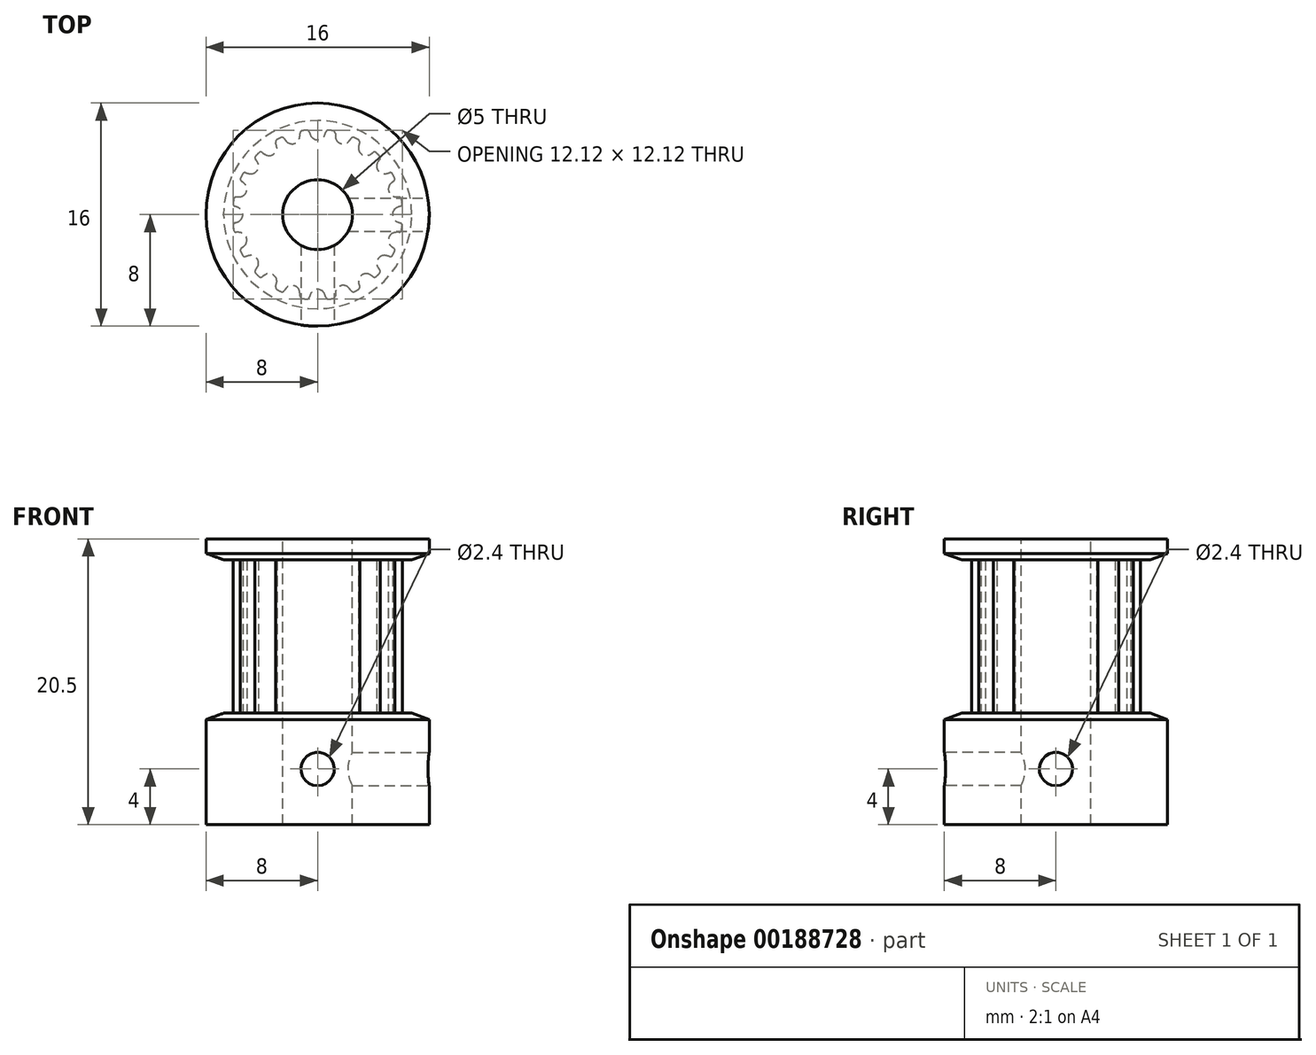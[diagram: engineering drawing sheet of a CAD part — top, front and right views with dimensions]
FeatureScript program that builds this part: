
annotation { "Feature Type Name" : "Feature", "Feature Type Description" : "" }
export const myFeature = defineFeature(function(context is Context, id is Id, definition is map)
    precondition{}
    {
        {
            assignVariable(context, id + "F0", {"name" : "teeth", "anyValue" : 20});
        }
        {
            assignVariable(context, id + "F1", {"name" : "bore_diameter", "anyValue" : 5 * mm});
        }
        {
            var Q0;
            Q0=qCreatedBy(makeId("Top.planeOp"),FACE);
            var sketch = newSketch(context, id + "F2", { "sketchPlane" : qUnion([Q0])});
            skLineSegment(sketch, "E0", {"start": v(0, 0) * mm, "end": v(0, 5.36) * mm, "construction": true});
            skCircle(sketch, "E1", {"center": v(0, 0) * mm, "radius": 6.11 * mm});
            skPoint(sketch, "E2.MirrorCS.end.orphan", {"position": v(0.96, 6.04) * mm});
            skLineSegment(sketch, "E3", {"start": v(0.96, 6.04) * mm, "end": v(1, 6.29) * mm, "construction": true});
            skLineSegment(sketch, "E4", {"start": v(-0.96, 6.04) * mm, "end": v(-1, 6.29) * mm, "construction": true});
            skArc(sketch, "E5", {"start": v(0, 5.36) * mm, "mid": v(0.31, 5.46) * mm, "end": v(0.52, 5.72) * mm});
            skArc(sketch, "E6", {"start": v(0.52, 5.72) * mm, "mid": v(0.56, 5.83) * mm, "end": v(0.58, 5.94) * mm, "construction": true});
            skLineSegment(sketch, "E7", {"start": v(0, 5.36) * mm, "end": v(0, 6.11) * mm, "construction": true});
            skLineSegment(sketch, "E8", {"start": v(0, 6.11) * mm, "end": v(0, 6.37) * mm, "construction": true});
            skArc(sketch, "E9", {"start": v(0.58, 5.94) * mm, "mid": v(0.64, 6.04) * mm, "end": v(0.75, 6.07) * mm, "construction": true});
            skArc(sketch, "E10", {"start": v(1, 6.29) * mm, "mid": v(0, 6.37) * mm, "end": v(-1, 6.29) * mm, "construction": true});
            skLineSegment(sketch, "E11", {"start": v(0.96, 6.04) * mm, "end": v(0.84, 5.3) * mm});
            skLineSegment(sketch, "E12", {"start": v(0.84, 5.3) * mm, "end": v(0, 0) * mm});
            skLineSegment(sketch, "E13", {"start": v(0, 0) * mm, "end": v(-0.84, 5.3) * mm});
            skLineSegment(sketch, "E14", {"start": v(-0.84, 5.3) * mm, "end": v(-0.96, 6.04) * mm});
            skArc(sketch, "E15", {"start": v(0.8, 6.06) * mm, "mid": v(0.67, 6.03) * mm, "end": v(0.6, 5.93) * mm});
            skArc(sketch, "E16", {"start": v(0.52, 5.72) * mm, "mid": v(0.56, 5.83) * mm, "end": v(0.6, 5.93) * mm});
            skArc(sketch, "E17.MirrorCS", {"start": v(0, 5.36) * mm, "mid": v(-0.31, 5.46) * mm, "end": v(-0.52, 5.72) * mm});
            skArc(sketch, "E18.MirrorCS", {"start": v(-0.52, 5.72) * mm, "mid": v(-0.56, 5.83) * mm, "end": v(-0.6, 5.93) * mm});
            skArc(sketch, "E19.MirrorCS", {"start": v(-0.8, 6.06) * mm, "mid": v(-0.67, 6.03) * mm, "end": v(-0.6, 5.93) * mm});
            skArc(sketch, "E20", {"start": v(0, 6.11) * mm, "mid": v(-0.2, 6.1) * mm, "end": v(-0.4, 6.1) * mm});
            skArc(sketch, "E21", {"start": v(0.84, 5.3) * mm, "mid": v(0, 5.36) * mm, "end": v(-0.84, 5.3) * mm, "construction": true});
            skLineSegment(sketch, "E22", {"start": v(1, 6.29) * mm, "end": v(1.05, 6.66) * mm, "construction": true});
            skLineSegment(sketch, "E23", {"start": v(-1, 6.29) * mm, "end": v(-1.05, 6.66) * mm, "construction": true});
            skArc(sketch, "E24", {"start": v(-1.05, 6.66) * mm, "mid": v(0, 6.74) * mm, "end": v(1.05, 6.66) * mm, "construction": true});
            skSolve(sketch);
        }
        {
            var Q0;
            Q0=makeQuery(id+"F2.imprint","IMPRINT",FACE,{"disambiguationData":[TD([[makeQuery(id+"F2.imprint","IMPRINT",EDGE,{"derivedFrom":sQuery(id+"F2.wireOp",EDGE,"E5")}),-1.0]])]});
            var Q1;
            {var subQ1=sQuery(id+"F2.wireOp",EDGE,"E14");Q1=makeQuery(id+"F2.imprint","IMPRINT",FACE,{"disambiguationData":[TD([[makeQuery(id+"F2.imprint","IMPRINT",EDGE,{"derivedFrom":subQ1}),-1.0]])]});}
            var Q2;
            {var subQ0=sQuery(id+"F2.wireOp",EDGE,"E12");Q2=makeQuery(id+"F2.imprint","IMPRINT",FACE,{"disambiguationData":[TD([[makeQuery(id+"F2.imprint","IMPRINT",EDGE,{"derivedFrom":subQ0}),-1.0]])]});}
            extrude(context, id + "F3", {"entities" : qUnion([Q0, Q1, Q2]), "depth" : 11 * mm, "symmetric" : true});
        }
        {
            var Q0;
            Q0=makeQuery(id+"F3.opExtrude","SWEPT_BODY",BODY,{"disambiguationData":[OSD([sQuery(id+"F2.wireOp",EDGE,"E1"),sQuery(id+"F2.wireOp",EDGE,"E5"),sQuery(id+"F2.wireOp",EDGE,"E11"),sQuery(id+"F2.wireOp",EDGE,"E12"),sQuery(id+"F2.wireOp",EDGE,"E13"),sQuery(id+"F2.wireOp",EDGE,"E14"),sQuery(id+"F2.wireOp",EDGE,"E15"),sQuery(id+"F2.wireOp",EDGE,"E16"),sQuery(id+"F2.wireOp",EDGE,"E17.MirrorCS"),sQuery(id+"F2.wireOp",EDGE,"E18.MirrorCS"),sQuery(id+"F2.wireOp",EDGE,"E19.MirrorCS")])]});
            var Q1;
            Q1=makeQuery(id+"F3.opExtrude","SWEPT_EDGE",EDGE,{"disambiguationData":[OSD([sQuery(id+"F2.wireOp",EDGE,"E12"),sQuery(id+"F2.wireOp",EDGE,"E13")])]});
            circularPattern(context, id + "F4", {"operationType" : NewBodyOperationType.ADD, "entities" : qUnion([Q0]), "axis" : qUnion([Q1]), "angle" : 360 * degree, "instanceCount" : getVariable(context, 'teeth'), "equalSpace" : true, "computeTransformsWithoutBuiltin" : true});
        }
        {
            var Q0;
            Q0=qCreatedBy(makeId("Front.planeOp"),FACE);
            var sketch = newSketch(context, id + "F5", { "sketchPlane" : qUnion([Q0])});
            skLineSegment(sketch, "E25", {"start": v(0, -5.5) * mm, "end": v(6.74, -5.5) * mm});
            skLineSegment(sketch, "E26", {"start": v(6.74, -5.5) * mm, "end": v(8, -5.96) * mm});
            skLineSegment(sketch, "E27", {"start": v(8, -5.96) * mm, "end": v(8, -13.5) * mm});
            skLineSegment(sketch, "E28", {"start": v(8, -13.5) * mm, "end": v(0, -13.5) * mm});
            skLineSegment(sketch, "E29", {"start": v(0, -13.5) * mm, "end": v(0, -5.5) * mm});
            skLineSegment(sketch, "E30", {"start": v(0, 5.5) * mm, "end": v(6.74, 5.5) * mm});
            skLineSegment(sketch, "E31", {"start": v(8, 5.96) * mm, "end": v(6.74, 5.5) * mm});
            skLineSegment(sketch, "E32", {"start": v(8, 5.96) * mm, "end": v(8, 7) * mm});
            skLineSegment(sketch, "E33", {"start": v(8, 7) * mm, "end": v(0, 7) * mm});
            skLineSegment(sketch, "E34", {"start": v(0, 7) * mm, "end": v(0, 5.5) * mm});
            skLineSegment(sketch, "E35", {"start": v(6.74, -5.5) * mm, "end": v(8, -5.5) * mm, "construction": true});
            skLineSegment(sketch, "E36", {"start": v(8, -5.5) * mm, "end": v(8, -5.96) * mm, "construction": true});
            skLineSegment(sketch, "E37", {"start": v(6.74, 5.5) * mm, "end": v(8, 5.5) * mm, "construction": true});
            skLineSegment(sketch, "E38", {"start": v(8, 5.5) * mm, "end": v(8, 5.96) * mm, "construction": true});
            skLineSegment(sketch, "E39", {"start": v(6.11, 0) * mm, "end": v(6.11, -5.5) * mm, "construction": true});
            skSolve(sketch);
        }
        {
            var Q0;
            Q0=qSketchRegion(id+"F5",true);
            var Q1;
            Q1=qConstructionFilter(qBodyType(qCreatedBy(id+"F5",EDGE),BodyType.WIRE),ConstructionObject.NO);
            var Q2;
            Q2=sQuery(id+"F5.wireOp",EDGE,"E29");
            revolve(context, id + "F6", {"operationType" : NewBodyOperationType.ADD, "entities" : qUnion([Q0]), "surfaceEntities" : qUnion([Q1]), "axis" : qUnion([Q2]), "revolveType" : RevolveType.FULL});
        }
        {
            var Q0;
            Q0=makeQuery(id+"F6.opRevolve","SWEPT_FACE",FACE,{"disambiguationData":[OSD([sQuery(id+"F5.wireOp",EDGE,"E28")])]});
            var sketch = newSketch(context, id + "F7", { "sketchPlane" : qUnion([Q0])});
            skPoint(sketch, "E40", {"position": v(0, 0) * mm});
            skSolve(sketch);
        }
        {
            var Q0;
            Q0=sQuery(id+"F7.wireOp",VERTEX,"E40");
            var Q1;
            Q1=makeQuery(id+"F3.opExtrude","SWEPT_BODY",BODY,{"disambiguationData":[OSD([sQuery(id+"F2.wireOp",EDGE,"E1"),sQuery(id+"F2.wireOp",EDGE,"E5"),sQuery(id+"F2.wireOp",EDGE,"E11"),sQuery(id+"F2.wireOp",EDGE,"E12"),sQuery(id+"F2.wireOp",EDGE,"E13"),sQuery(id+"F2.wireOp",EDGE,"E14"),sQuery(id+"F2.wireOp",EDGE,"E15"),sQuery(id+"F2.wireOp",EDGE,"E16"),sQuery(id+"F2.wireOp",EDGE,"E17.MirrorCS"),sQuery(id+"F2.wireOp",EDGE,"E18.MirrorCS"),sQuery(id+"F2.wireOp",EDGE,"E19.MirrorCS")])]});
            hole(context, id + "F8", {"style" : HoleStyle.SIMPLE, "holeDiameter" : getVariable(context, 'bore_diameter'), "endStyle" : HoleEndStyle.THROUGH, "locations" : qUnion([Q0]), "scope" : qUnion([Q1]), "isTappedThrough" : true, "startStyle" : HoleStartStyle.PART});
        }
        {
            var Q0;
            Q0=qCreatedBy(makeId("Front.planeOp"),FACE);
            var sketch = newSketch(context, id + "F9", { "sketchPlane" : qUnion([Q0])});
            skPoint(sketch, "E41", {"position": v(0, -9.5) * mm});
            skLineSegment(sketch, "E42", {"start": v(0, -13.5) * mm, "end": v(0, -5.5) * mm});
            skSolve(sketch);
        }
        {
            var Q0;
            Q0=qCreatedBy(makeId("Right.planeOp"),FACE);
            var sketch = newSketch(context, id + "F10", { "sketchPlane" : qUnion([Q0])});
            skPoint(sketch, "E43", {"position": v(0, -9.5) * mm});
            skSolve(sketch);
        }
        {
            var Q0;
            Q0=sQuery(id+"F9.wireOp",VERTEX,"E41");
            var Q1;
            Q1=makeQuery(id+"F3.opExtrude","SWEPT_BODY",BODY,{"disambiguationData":[OSD([sQuery(id+"F2.wireOp",EDGE,"E1"),sQuery(id+"F2.wireOp",EDGE,"E5"),sQuery(id+"F2.wireOp",EDGE,"E11"),sQuery(id+"F2.wireOp",EDGE,"E12"),sQuery(id+"F2.wireOp",EDGE,"E13"),sQuery(id+"F2.wireOp",EDGE,"E14"),sQuery(id+"F2.wireOp",EDGE,"E15"),sQuery(id+"F2.wireOp",EDGE,"E16"),sQuery(id+"F2.wireOp",EDGE,"E17.MirrorCS"),sQuery(id+"F2.wireOp",EDGE,"E18.MirrorCS"),sQuery(id+"F2.wireOp",EDGE,"E19.MirrorCS")])]});
            hole(context, id + "F11", {"style" : HoleStyle.SIMPLE, "endStyle" : HoleEndStyle.THROUGH, "oppositeDirection" : true, "standardTappedOrClearance" : lookupTablePath({ "standard" : "ISO", "engagement" : "75%", "pitch" : "0.6 mm", "size" : "M3", "type" : "Tapped" }), "standardBlindInLast" : lookupTablePath({ "standard" : "ISO", "engagement" : "75%", "pitch" : "0.6 mm", "size" : "M3", "type" : "Tapped" }), "holeDiameter" : 2.4 * mm, "locations" : qUnion([Q0]), "scope" : qUnion([Q1]), "isTappedThrough" : true, "showTappedDepth" : true, "startStyle" : HoleStartStyle.PART});
        }
        {
            var Q0;
            Q0=sQuery(id+"F10.wireOp",VERTEX,"E43");
            var Q1;
            Q1=makeQuery(id+"F3.opExtrude","SWEPT_BODY",BODY,{"disambiguationData":[OSD([sQuery(id+"F2.wireOp",EDGE,"E1"),sQuery(id+"F2.wireOp",EDGE,"E5"),sQuery(id+"F2.wireOp",EDGE,"E11"),sQuery(id+"F2.wireOp",EDGE,"E12"),sQuery(id+"F2.wireOp",EDGE,"E13"),sQuery(id+"F2.wireOp",EDGE,"E14"),sQuery(id+"F2.wireOp",EDGE,"E15"),sQuery(id+"F2.wireOp",EDGE,"E16"),sQuery(id+"F2.wireOp",EDGE,"E17.MirrorCS"),sQuery(id+"F2.wireOp",EDGE,"E18.MirrorCS"),sQuery(id+"F2.wireOp",EDGE,"E19.MirrorCS")])]});
            hole(context, id + "F12", {"style" : HoleStyle.SIMPLE, "endStyle" : HoleEndStyle.THROUGH, "oppositeDirection" : true, "standardTappedOrClearance" : lookupTablePath({ "standard" : "ISO", "engagement" : "75%", "pitch" : "0.6 mm", "size" : "M3", "type" : "Tapped" }), "standardBlindInLast" : lookupTablePath({ "standard" : "ISO", "engagement" : "75%", "pitch" : "0.6 mm", "size" : "M3", "type" : "Tapped" }), "holeDiameter" : 2.4 * mm, "locations" : qUnion([Q0]), "scope" : qUnion([Q1]), "isTappedThrough" : true, "showTappedDepth" : true, "startStyle" : HoleStartStyle.PART});
        }
    });
